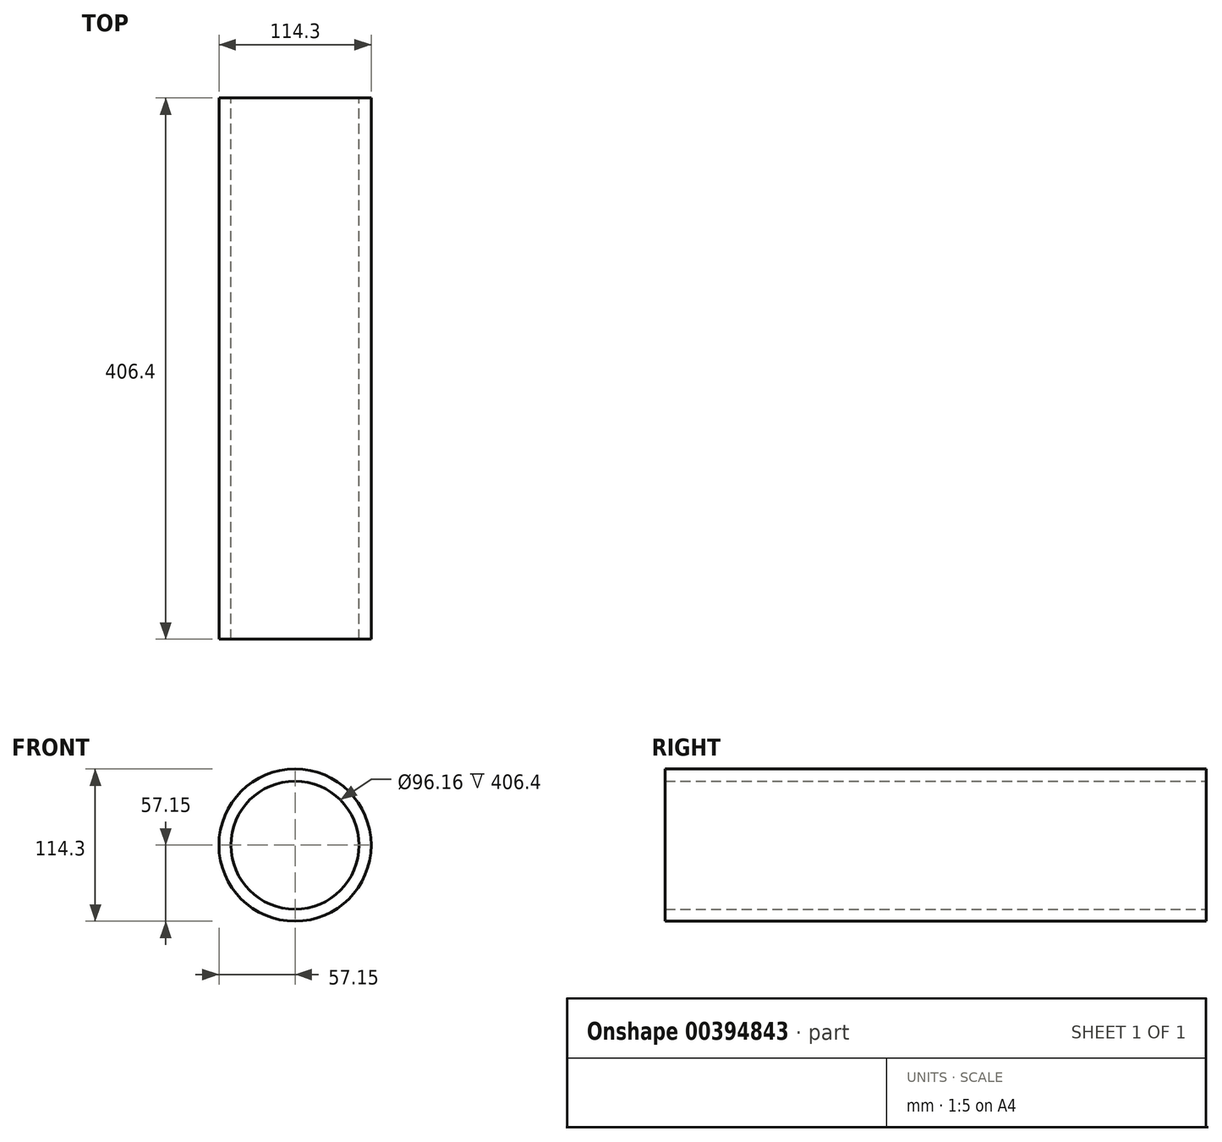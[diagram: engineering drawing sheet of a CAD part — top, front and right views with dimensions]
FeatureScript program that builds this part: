
annotation { "Feature Type Name" : "Feature", "Feature Type Description" : "" }
export const myFeature = defineFeature(function(context is Context, id is Id, definition is map)
    precondition{}
    {
        {
            var Q0;
            Q0=qCreatedBy(makeId("Front.planeOp"),FACE);
            var sketch = newSketch(context, id + "F0", { "sketchPlane" : qUnion([Q0])});
            skCircle(sketch, "E0", {"center": v(0, 0) * mm, "radius": 57.15 * mm});
            skCircle(sketch, "E1", {"center": v(0, 0) * mm, "radius": 48.08 * mm});
            skSolve(sketch);
        }
        {
            var Q0;
            Q0=qSketchRegion(id+"F0",true);
            extrude(context, id + "F1", {"entities" : qUnion([Q0]), "depth" : 406.4 * mm});
        }
    });
